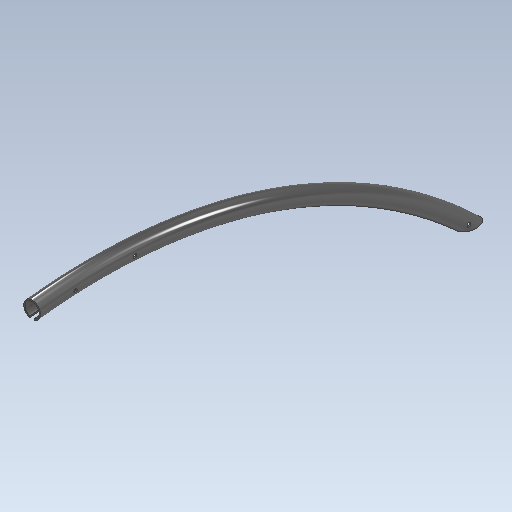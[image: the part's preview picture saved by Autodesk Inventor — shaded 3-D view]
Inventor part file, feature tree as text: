
AUTODESK INVENTOR PART (.ipt)
format: ipt  version: 2021 (Build 250183000, 183)  size: 318,976 bytes
history: native  units: mm
features: other x6, sketch x5, extrude x3, sweep x2, split x1, hole x1
ambient origin geometry x8: Origin, YZ Plane, XZ Plane, XY Plane, X Axis, Y Axis, Z Axis, Center Point
bodies: Solid1 (feature_tree)
feature tree (18):
  sketch  "Sketch1"  dims[d0=3300.0mm d1=1650.0mm]
  sweep  "Sweep1"
  sweep  "Sweep2"
  extrude  "Extrusion1"  Depth=43.0mm
  extrude  "Extrusion3"  Depth=1650.0mm
  other  "fea_loadSplit"
  split  "Split1"
  other  "midPlane"
  extrude  "Extrusion4"  Depth=6.0mm
  other  "tabHolePositioning"
  other  "midTabPlane"
  other  "projCentreAxis"
  other  "centreCut"
  hole  "tabHoles"  [1 undecoded]
  sketch  "Sketch2"  dims[d2=0.0mm d3=51.0mm]
  sketch  "Sketch3"  dims[d4=0.0mm d5=0.0mm d6=43.0mm]
  sketch  "Sketch4"  dims[d7=0.0mm d8=1650.0mm]
  sketch  "Sketch7"  dims[d9=0.0mm d10=0.0mm d11=1752.0mm d12=3402.0mm d13=1701.0mm d14=1200.0mm d15=1701.0mm d16=1701.0mm d17=200.0mm d18=51.0mm d19=0.0mm d22=14.0mm d23=0.0mm d24=-144.0mm d25=10.0mm d26=3300.0mm d27=100.0mm d28=0.0mm d34=3300.0mm d35=1200.0mm d36=1050.1mm d37=0.0mm d38=3300.0mm d39=1200.0mm d40=0.0mm d41=25.0mm d42=12.0mm d43=6.0mm d44=4.0mm d45=2.0mm d46=90.0deg d47=8.0mm d48=20.594885mm]
note: 1 required parameter value undecoded (feature->parameter linkage not recoverable at this tier; creation-order binding heuristic only, values carry confidence <= 0.55)
